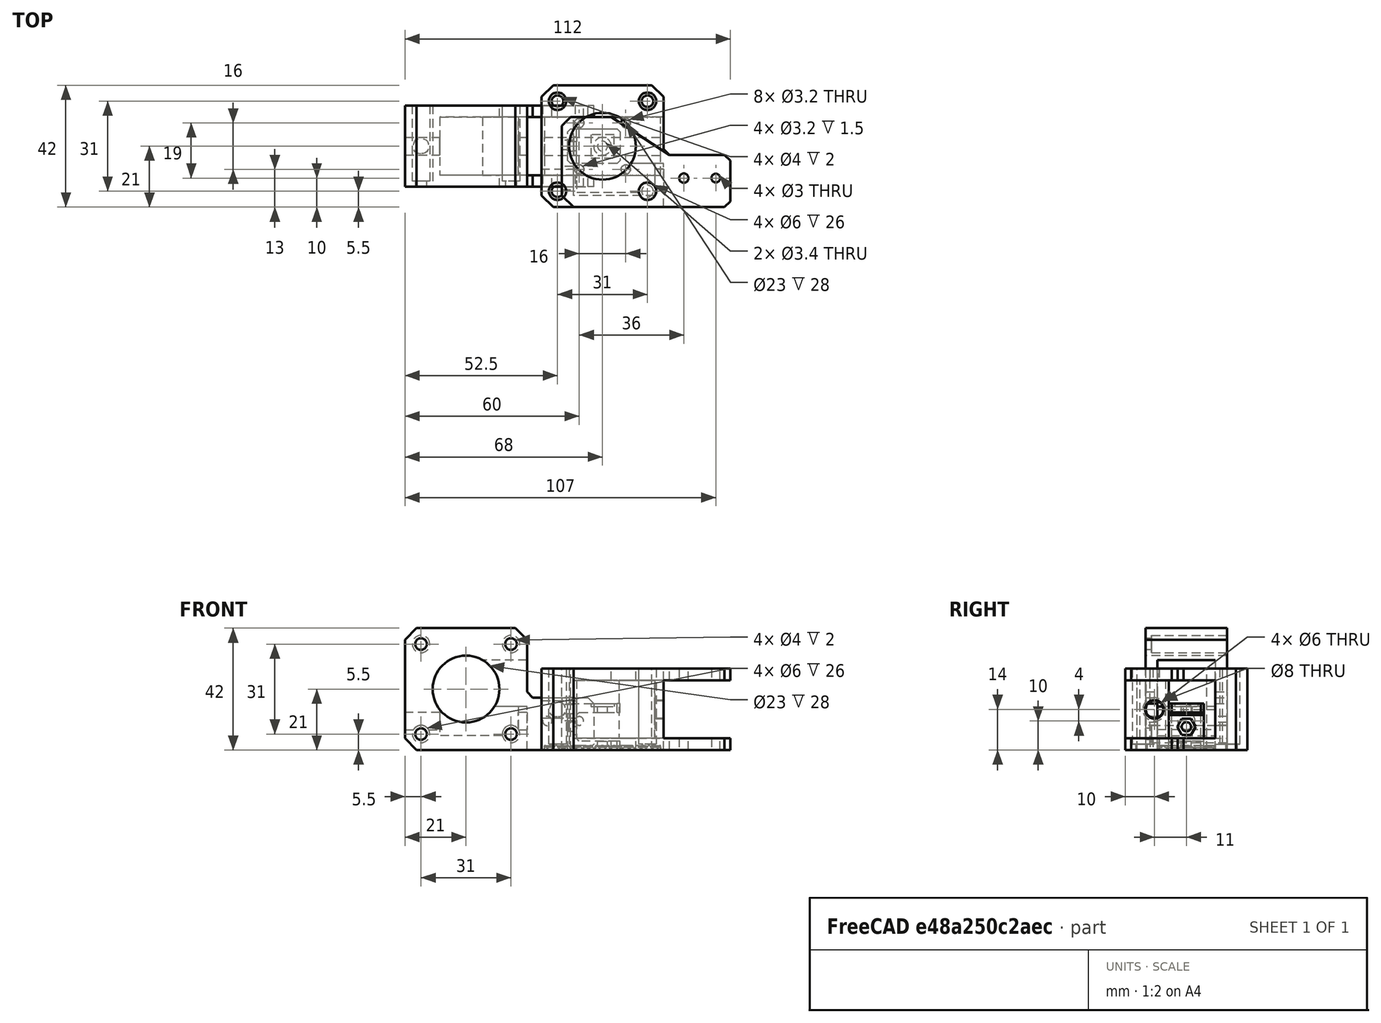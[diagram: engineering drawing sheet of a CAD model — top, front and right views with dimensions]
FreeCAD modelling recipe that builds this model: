
FCSTD DOCUMENT  (FreeCAD 1.0R39285 (Git))
Label: LinearRailMod
License: All rights reserved
LicenseURL: https://en.wikipedia.org/wiki/All_rights_reserved
objects: Sketcher::SketchObject×23, PartDesign::Pocket×18, PartDesign::Pad×5, PartDesign::Body×5, App::Part×5, Part::Mirroring×1, PartDesign::Hole×1, Assembly::JointGroup×1, Assembly::AssemblyObject×1
note: 124 computed .brp shape members not serialized (recipe doc carries the construction recipe); baked Part::Feature solids carry a one-line shape summary decoded from their .brp

FEATURE [Sketcher::SketchObject] Sketch
  ArcFitTolerance = 1e-06
  AttachmentSupport = -> [XY_Plane001]
  FullyConstrained = false
  MakeInternals = false
  MapMode = 5
  sketch-geometry (20):
    g0: GeomPoint [constr] X=0 Y=0 Z=0
    g1: LineSegment StartX=-17 StartY=21 StartZ=0 EndX=-21 EndY=17 EndZ=0
    g2: LineSegment StartX=-21 StartY=-17 StartZ=0 EndX=-17 EndY=-21 EndZ=0
    g3: LineSegment StartX=17 StartY=21 StartZ=0 EndX=21 EndY=17 EndZ=0
    g4: Circle CenterX=-15.5 CenterY=-15.5 CenterZ=0 NormalX=0 NormalY=0 NormalZ=1 AngleXU=0 Radius=2
    g5: Circle CenterX=15.5 CenterY=-15.5 CenterZ=0 NormalX=0 NormalY=0 NormalZ=1 AngleXU=0 Radius=2
    g6: Circle CenterX=15.5 CenterY=15.5 CenterZ=0 NormalX=0 NormalY=0 NormalZ=1 AngleXU=0 Radius=2
    g7: LineSegment StartX=-21 StartY=17 StartZ=0 EndX=-21 EndY=-17 EndZ=0
    g8: LineSegment StartX=-17 StartY=-21 StartZ=0 EndX=42 EndY=-21 EndZ=0
    g9: LineSegment StartX=-17 StartY=21 StartZ=0 EndX=17 EndY=21 EndZ=0
    g10: LineSegment StartX=21 StartY=17 StartZ=0 EndX=21 EndY=-1 EndZ=0
    g11: LineSegment StartX=44 StartY=-19 StartZ=0 EndX=42 EndY=-21 EndZ=0
    g12: Circle CenterX=-15.5 CenterY=15.5 CenterZ=0 NormalX=0 NormalY=0 NormalZ=1 AngleXU=0 Radius=2
    g13: Circle CenterX=0 CenterY=0 CenterZ=0 NormalX=0 NormalY=0 NormalZ=1 AngleXU=0 Radius=11.5
    g14: Circle CenterX=28 CenterY=-11 CenterZ=0 NormalX=0 NormalY=0 NormalZ=1 AngleXU=0 Radius=1.6
    g15: LineSegment StartX=21 StartY=-1 StartZ=0 EndX=23 EndY=-3 EndZ=0
    g16: LineSegment StartX=23 StartY=-3 StartZ=0 EndX=42 EndY=-3 EndZ=0
    g17: LineSegment StartX=42 StartY=-3 StartZ=0 EndX=44 EndY=-5 EndZ=0
    g18: LineSegment StartX=44 StartY=-5 StartZ=0 EndX=44 EndY=-19 EndZ=0
    g19: Circle CenterX=39 CenterY=-11 CenterZ=0 NormalX=0 NormalY=0 NormalZ=1 AngleXU=0 Radius=1.5
  constraints (19):
    c: Coincident(g7,g1)
    c: Coincident(g7,g2)
    c: Vertical(g7)
    c: Coincident(g8,g2)
    c: Horizontal(g8)
    c: Coincident(g9,g1)
    c: Coincident(g9,g3)
    c: Horizontal(g9)
    c: Coincident(g10,g3)
    c: Vertical(g10)
    c: Coincident(g11,g8)
    c: Coincident(g13,g0)
    c: Coincident(g15,g10)
    c: Coincident(g16,g15)
    c: Horizontal(g16)
    c: Coincident(g17,g16)
    c: Coincident(g18,g17)
    c: Coincident(g18,g11)
    c: Vertical(g18)
FEATURE [PartDesign::Pad] Pad
  Direction = (0,0,1)
  Length = 28
  Length2 = 10
  Profile = -> Sketch
  ReferenceAxis = -> Sketch [N_Axis]
  Refine = true
  Suppressed = false
  Type = 0
FEATURE [Sketcher::SketchObject] Sketch003
  ArcFitTolerance = 1e-06
  AttachmentSupport = -> [Pad]
  FullyConstrained = false
  MakeInternals = false
  MapMode = 5
  Placement = pos=(0,-21,0) rot=(1,0,0;1.5708rad)
  sketch-geometry (4):
    g0: LineSegment StartX=21 StartY=24 StartZ=0 EndX=21 EndY=4 EndZ=0
    g1: LineSegment StartX=21 StartY=4 StartZ=0 EndX=50 EndY=4 EndZ=0
    g2: LineSegment StartX=50 StartY=4 StartZ=0 EndX=50 EndY=24 EndZ=0
    g3: LineSegment StartX=50 StartY=24 StartZ=0 EndX=21 EndY=24 EndZ=0
  constraints (8):
    c: Coincident(g0,g1)
    c: Coincident(g1,g2)
    c: Coincident(g2,g3)
    c: Coincident(g3,g0)
    c: Vertical(g0)
    c: Vertical(g2)
    c: Horizontal(g1)
    c: Horizontal(g3)
FEATURE [PartDesign::Pocket] Pocket
  BaseFeature = -> Pad
  Direction = (0,1,-2e-16)
  Length = 42
  Length2 = 5
  Profile = -> Sketch003
  ReferenceAxis = -> Sketch003 [N_Axis]
  Refine = true
  Suppressed = false
  Type = 0
FEATURE [Sketcher::SketchObject] Sketch004
  ArcFitTolerance = 1e-06
  AttachmentSupport = -> [Pocket]
  FullyConstrained = false
  MakeInternals = false
  MapMode = 5
  Placement = pos=(0,0,28) rot=(0,0,1;0rad)
  sketch-geometry (4):
    g0: Circle CenterX=-15.5 CenterY=-15.5 CenterZ=0 NormalX=0 NormalY=0 NormalZ=1 AngleXU=0 Radius=3
    g1: Circle CenterX=-15.5 CenterY=15.5 CenterZ=0 NormalX=0 NormalY=0 NormalZ=1 AngleXU=0 Radius=3
    g2: Circle CenterX=15.5 CenterY=15.5 CenterZ=0 NormalX=0 NormalY=0 NormalZ=1 AngleXU=0 Radius=3
    g3: Circle CenterX=15.5 CenterY=-15.5 CenterZ=0 NormalX=0 NormalY=0 NormalZ=1 AngleXU=0 Radius=3
FEATURE [PartDesign::Pocket] Pocket001
  BaseFeature = -> Pocket
  Direction = (0,0,-1)
  Length = 26
  Length2 = 5
  Profile = -> Sketch004
  ReferenceAxis = -> Sketch004 [N_Axis]
  Refine = true
  Suppressed = false
  Type = 0
FEATURE [Sketcher::SketchObject] Sketch005
  ArcFitTolerance = 1e-06
  AttachmentSupport = -> [Pocket001]
  FullyConstrained = false
  MakeInternals = false
  MapMode = 5
  Placement = pos=(21,0,0) rot=(0.57735,0.57735,0.57735;2.0944rad)
  sketch-geometry (1):
    g0: Circle CenterX=-11 CenterY=14 CenterZ=0 NormalX=0 NormalY=0 NormalZ=1 AngleXU=0 Radius=3
FEATURE [PartDesign::Pocket] Pocket002
  BaseFeature = -> Pocket001
  Direction = (-1,0,0)
  Length = 42
  Length2 = 5
  Profile = -> Sketch005
  ReferenceAxis = -> Sketch005 [N_Axis]
  Refine = true
  Suppressed = false
  Type = 0
FEATURE [Sketcher::SketchObject] Sketch006
  ArcFitTolerance = 1e-06
  AttachmentSupport = -> [Pocket002]
  FullyConstrained = false
  MakeInternals = false
  MapMode = 5
  Placement = pos=(21,0,0) rot=(0.57735,0.57735,0.57735;2.0944rad)
  sketch-geometry (4):
    g0: LineSegment StartX=-6 StartY=24 StartZ=0 EndX=-6 EndY=4 EndZ=0
    g1: LineSegment StartX=-6 StartY=4 StartZ=0 EndX=10 EndY=4 EndZ=0
    g2: LineSegment StartX=10 StartY=4 StartZ=0 EndX=10 EndY=24 EndZ=0
    g3: LineSegment StartX=10 StartY=24 StartZ=0 EndX=-6 EndY=24 EndZ=0
  constraints (8):
    c: Coincident(g0,g1)
    c: Coincident(g1,g2)
    c: Coincident(g2,g3)
    c: Coincident(g3,g0)
    c: Vertical(g0)
    c: Vertical(g2)
    c: Horizontal(g1)
    c: Horizontal(g3)
FEATURE [PartDesign::Pocket] Pocket003
  BaseFeature = -> Pocket002
  Direction = (-1,0,0)
  Length = 16
  Length2 = 5
  Profile = -> Sketch006
  ReferenceAxis = -> Sketch006 [N_Axis]
  Refine = true
  Suppressed = false
  Type = 0
FEATURE [Sketcher::SketchObject] Sketch007
  ArcFitTolerance = 1e-06
  AttachmentSupport = -> [Pocket003]
  FullyConstrained = false
  MakeInternals = false
  MapMode = 5
  Placement = pos=(0,-6,0) rot=(0,0.707107,0.707107;3.14159rad)
  sketch-geometry (4):
    g0: LineSegment StartX=-18 StartY=24.038 StartZ=0 EndX=-18 EndY=4.03804 EndZ=0
    g1: LineSegment StartX=-18 StartY=4.03804 StartZ=0 EndX=9 EndY=4.03804 EndZ=0
    g2: LineSegment StartX=9 StartY=4.03804 StartZ=0 EndX=9 EndY=24.038 EndZ=0
    g3: LineSegment StartX=9 StartY=24.038 StartZ=0 EndX=-18 EndY=24.038 EndZ=0
  constraints (8):
    c: Coincident(g0,g1)
    c: Coincident(g1,g2)
    c: Coincident(g2,g3)
    c: Coincident(g3,g0)
    c: Vertical(g0)
    c: Vertical(g2)
    c: Horizontal(g1)
    c: Horizontal(g3)
FEATURE [PartDesign::Pocket] Pocket004
  BaseFeature = -> Pocket003
  Direction = (0,-1,2e-16)
  Length = 10
  Length2 = 5
  Profile = -> Sketch007
  ReferenceAxis = -> Sketch007 [N_Axis]
  Refine = true
  Suppressed = false
  Type = 0
FEATURE [PartDesign::Body] Body
  AllowCompound = false
  Group = -> [Sketch,Pad,Sketch003,Pocket,Sketch004,Pocket001,Sketch005,Pocket002,Sketch006,Pocket003,Sketch007,Pocket004]
  Origin = -> Origin001
  Tip = -> Pocket004
FEATURE [App::Part] Part  label="Motor"
  Group = -> [Body]
  Origin = -> Origin
  Placement = pos=(-47,-41,21) rot=(1,0,0;1.5708rad)
FEATURE [Sketcher::SketchObject] Sketch008
  ArcFitTolerance = 1e-06
  AttachmentSupport = -> [XY_Plane007]
  FullyConstrained = false
  MakeInternals = false
  MapMode = 5
  sketch-geometry (12):
    g0: LineSegment StartX=-14 StartY=-17 StartZ=0 EndX=-10 EndY=-21 EndZ=0
    g1: LineSegment StartX=-14 StartY=7 StartZ=0 EndX=-14 EndY=-17 EndZ=0
    g2: LineSegment StartX=-10 StartY=-21 StartZ=0 EndX=42 EndY=-21 EndZ=0
    g3: LineSegment StartX=44 StartY=-19 StartZ=0 EndX=42 EndY=-21 EndZ=0
    g4: Circle CenterX=28 CenterY=-11 CenterZ=0 NormalX=0 NormalY=0 NormalZ=1 AngleXU=0 Radius=1.6
    g5: LineSegment StartX=23 StartY=-3 StartZ=0 EndX=42 EndY=-3 EndZ=0
    g6: LineSegment StartX=42 StartY=-3 StartZ=0 EndX=44 EndY=-5 EndZ=0
    g7: LineSegment StartX=44 StartY=-5 StartZ=0 EndX=44 EndY=-19 EndZ=0
    g8: Circle CenterX=39 CenterY=-11 CenterZ=0 NormalX=0 NormalY=0 NormalZ=1 AngleXU=0 Radius=1.5
    g9: LineSegment StartX=23 StartY=-3 StartZ=0 EndX=3 EndY=10 EndZ=0
    g10: LineSegment StartX=3 StartY=10 StartZ=0 EndX=-11 EndY=10 EndZ=0
    g11: LineSegment StartX=-11 StartY=10 StartZ=0 EndX=-14 EndY=7 EndZ=0
  constraints (15):
    c: Coincident(g1,g0)
    c: Vertical(g1)
    c: Coincident(g2,g0)
    c: Horizontal(g2)
    c: Coincident(g3,g2)
    c: Horizontal(g5)
    c: Coincident(g6,g5)
    c: Coincident(g7,g6)
    c: Coincident(g7,g3)
    c: Vertical(g7)
    c: Coincident(g5,g9)
    c: Coincident(g9,g10)
    c: Horizontal(g10)
    c: Coincident(g10,g11)
    c: Coincident(g11,g1)
FEATURE [Sketcher::SketchObject] Sketch009
  ArcFitTolerance = 1e-06
  AttachmentSupport = -> [XY_Plane006]
  FullyConstrained = false
  MakeInternals = false
  MapMode = 5
  sketch-geometry (10):
    g0: Circle [constr] CenterX=0 CenterY=0 CenterZ=0 NormalX=0 NormalY=0 NormalZ=1 AngleXU=0 Radius=6.5
    g1: LineSegment StartX=-12 StartY=5 StartZ=0 EndX=-11 EndY=6 EndZ=0
    g2: LineSegment StartX=-11 StartY=6 StartZ=0 EndX=5 EndY=6 EndZ=0
    g3: LineSegment StartX=5 StartY=6 StartZ=0 EndX=6 EndY=5 EndZ=0
    g4: LineSegment StartX=6 StartY=5 StartZ=0 EndX=6 EndY=-5 EndZ=0
    g5: LineSegment StartX=6 StartY=-5 StartZ=0 EndX=5 EndY=-6 EndZ=0
    g6: LineSegment StartX=5 StartY=-6 StartZ=0 EndX=-11 EndY=-6 EndZ=0
    g7: LineSegment StartX=-11 StartY=-6 StartZ=0 EndX=-12 EndY=-5 EndZ=0
    g8: LineSegment StartX=-12 StartY=-5 StartZ=0 EndX=-12 EndY=5 EndZ=0
    g9: Circle CenterX=0 CenterY=0 CenterZ=0 NormalX=0 NormalY=0 NormalZ=1 AngleXU=0 Radius=1.6
  constraints (12):
    c: Coincident(g1,g2)
    c: Horizontal(g2)
    c: Coincident(g2,g3)
    c: Coincident(g3,g4)
    c: Vertical(g4)
    c: Coincident(g4,g5)
    c: Coincident(g5,g6)
    c: Horizontal(g6)
    c: Coincident(g6,g7)
    c: Coincident(g7,g8)
    c: Coincident(g8,g1)
    c: Vertical(g8)
FEATURE [Part::Mirroring] Part__Mirroring  label="Motor (Mirror #1)"
  Base = (0,0,0)
  Normal = (0,0,1)
  Placement = pos=(0,-55,2.04e-14) rot=(1,0,0;3.14159rad)
  Source = -> Part
FEATURE [PartDesign::Pad] Pad001
  Direction = (0,0,1)
  Length = 16
  Length2 = 10
  Profile = -> Sketch009
  ReferenceAxis = -> Sketch009 [N_Axis]
  Refine = true
  Suppressed = false
  Type = 0
FEATURE [Sketcher::SketchObject] Sketch013
  ArcFitTolerance = 1e-06
  FullyConstrained = false
  MakeInternals = false
  MapMode = 5
  Placement = pos=(0,-6,0) rot=(1,0,0;1.5708rad)
  sketch-geometry (6):
    g0: LineSegment StartX=-9 StartY=12 StartZ=0 EndX=-8 EndY=13 EndZ=0
    g1: LineSegment StartX=-8 StartY=13 StartZ=0 EndX=5 EndY=13 EndZ=0
    g2: LineSegment StartX=5 StartY=13 StartZ=0 EndX=5 EndY=3 EndZ=0
    g3: LineSegment StartX=5 StartY=3 StartZ=0 EndX=-8 EndY=3 EndZ=0
    g4: LineSegment StartX=-8 StartY=3 StartZ=0 EndX=-9 EndY=4 EndZ=0
    g5: LineSegment StartX=-9 StartY=4 StartZ=0 EndX=-9 EndY=12 EndZ=0
  constraints (10):
    c: Coincident(g0,g1)
    c: Horizontal(g1)
    c: Coincident(g1,g2)
    c: Vertical(g2)
    c: Coincident(g2,g3)
    c: Horizontal(g3)
    c: Coincident(g3,g4)
    c: Coincident(g4,g5)
    c: Coincident(g5,g0)
    c: Vertical(g5)
FEATURE [Sketcher::SketchObject] Sketch014
  ArcFitTolerance = 1e-06
  FullyConstrained = false
  MakeInternals = false
  MapMode = 5
  Placement = pos=(5,0,0) rot=(0.57735,-0.57735,-0.57735;2.0944rad)
  sketch-geometry (4):
    g0: LineSegment StartX=-6 StartY=13 StartZ=0 EndX=-6 EndY=3 EndZ=0
    g1: LineSegment StartX=-6 StartY=3 StartZ=0 EndX=6 EndY=3 EndZ=0
    g2: LineSegment StartX=6 StartY=3 StartZ=0 EndX=6 EndY=13 EndZ=0
    g3: LineSegment StartX=6 StartY=13 StartZ=0 EndX=-6 EndY=13 EndZ=0
  constraints (8):
    c: Coincident(g0,g1)
    c: Coincident(g1,g2)
    c: Coincident(g2,g3)
    c: Coincident(g3,g0)
    c: Vertical(g0)
    c: Vertical(g2)
    c: Horizontal(g1)
    c: Horizontal(g3)
FEATURE [PartDesign::Pocket] Pocket006
  BaseFeature = -> Pad001
  Direction = (0,1,-2e-16)
  Length = 12
  Length2 = 5
  Profile = -> Sketch013
  ReferenceAxis = -> Sketch013 [N_Axis]
  Refine = true
  Suppressed = false
  Type = 0
FEATURE [PartDesign::Pocket] Pocket007
  BaseFeature = -> Pocket006
  Direction = (1,-1e-16,1e-16)
  Length = 1
  Length2 = 5
  Profile = -> Sketch014
  ReferenceAxis = -> Sketch014 [N_Axis]
  Refine = true
  Suppressed = false
  Type = 0
FEATURE [Sketcher::SketchObject] Sketch015
  ArcFitTolerance = 1e-06
  AttachmentSupport = -> [Pocket007]
  FullyConstrained = false
  MakeInternals = false
  MapMode = 5
  Placement = pos=(-12,0,0) rot=(0.57735,-0.57735,-0.57735;2.0944rad)
  sketch-geometry (1):
    g0: Circle CenterX=0 CenterY=8 CenterZ=0 NormalX=0 NormalY=0 NormalZ=1 AngleXU=0 Radius=1.6
FEATURE [PartDesign::Pocket] Pocket008
  BaseFeature = -> Pocket007
  Direction = (1,0,0)
  Length = 3
  Length2 = 5
  Profile = -> Sketch015
  ReferenceAxis = -> Sketch015 [N_Axis]
  Refine = true
  Suppressed = false
  Type = 0
FEATURE [Sketcher::SketchObject] Sketch016
  ArcFitTolerance = 1e-06
  AttachmentSupport = -> [Pocket008]
  FullyConstrained = false
  MakeInternals = false
  MapMode = 5
  Placement = pos=(0,0,16) rot=(0,0,1;0rad)
  sketch-geometry (5):
    g0: LineSegment StartX=-4 StartY=-4 StartZ=0 EndX=4 EndY=-4 EndZ=0
    g1: LineSegment StartX=4 StartY=-4 StartZ=0 EndX=4 EndY=4 EndZ=0
    g2: LineSegment StartX=4 StartY=4 StartZ=0 EndX=-4 EndY=4 EndZ=0
    g3: LineSegment StartX=-4 StartY=4 StartZ=0 EndX=-4 EndY=-4 EndZ=0
    g4: GeomPoint [constr] X=0 Y=0 Z=0
  constraints (10):
    c: Coincident(g0,g1)
    c: Coincident(g1,g2)
    c: Coincident(g2,g3)
    c: Coincident(g3,g0)
    c: Horizontal(g0)
    c: Horizontal(g2)
    c: Vertical(g1)
    c: Vertical(g3)
    c: Symmetric(g2,g0,g4)
    c: Coincident(g4,g-1)
FEATURE [PartDesign::Pocket] Pocket009
  BaseFeature = -> Pocket008
  Direction = (0,0,-1)
  Length = 1
  Length2 = 5
  Profile = -> Sketch016
  ReferenceAxis = -> Sketch016 [N_Axis]
  Refine = true
  Suppressed = false
  Type = 0
FEATURE [Sketcher::SketchObject] Sketch017
  ArcFitTolerance = 1e-06
  AttachmentSupport = -> [Pocket009]
  FullyConstrained = false
  MakeInternals = false
  MapMode = 5
  Placement = pos=(-9,0,0) rot=(0.57735,0.57735,0.57735;2.0944rad)
  sketch-geometry (7):
    g0: LineSegment StartX=3.2 StartY=8 StartZ=0 EndX=1.6 EndY=10.7713 EndZ=0
    g1: LineSegment StartX=1.6 StartY=10.7713 StartZ=0 EndX=-1.6 EndY=10.7713 EndZ=0
    g2: LineSegment StartX=-1.6 StartY=10.7713 StartZ=0 EndX=-3.2 EndY=8 EndZ=0
    g3: LineSegment StartX=-3.2 StartY=8 StartZ=0 EndX=-1.6 EndY=5.22872 EndZ=0
    g4: LineSegment StartX=-1.6 StartY=5.22872 StartZ=0 EndX=1.6 EndY=5.22872 EndZ=0
    g5: LineSegment StartX=1.6 StartY=5.22872 StartZ=0 EndX=3.2 EndY=8 EndZ=0
    g6: Circle [constr] CenterX=0 CenterY=8 CenterZ=0 NormalX=0 NormalY=0 NormalZ=1 AngleXU=0 Radius=3.2
  constraints (13):
    c: Coincident(g0,g1)
    c: Coincident(g1,g2)
    c: Coincident(g2,g3)
    c: Coincident(g3,g4)
    c: Coincident(g4,g5)
    c: Coincident(g5,g0)
    c: Equal(g0, g1-g5) x5
    c: PointOnObject(g0,g6)
    c: PointOnObject(g1,g6)
    c: PointOnObject(g2,g6)
    c: PointOnObject(g3,g6)
    c: PointOnObject(g4,g6)
    c: PointOnObject(g5,g6)
FEATURE [PartDesign::Pocket] Pocket010
  BaseFeature = -> Pocket009
  Direction = (-1,0,0)
  Length = 1
  Length2 = 5
  Profile = -> Sketch017
  ReferenceAxis = -> Sketch017 [N_Axis]
  Refine = true
  Suppressed = false
  Type = 0
FEATURE [PartDesign::Hole] Hole
  BaseFeature = -> Pocket010
  CustomThreadClearance = 0
  Depth = 25
  DepthType = 0
  Diameter = 3.4
  DrillForDepth = false
  DrillPoint = 1
  DrillPointAngle = 118
  HoleCutCountersinkAngle = 90
  HoleCutCustomValues = false
  HoleCutDepth = 0
  HoleCutDiameter = 6.1
  HoleCutType = 2
  ModelThread = false
  Profile = -> Pocket010 [Face4]
  Refine = true
  Suppressed = false
  Tapered = false
  TaperedAngle = 90
  ThreadClass = 0
  ThreadDepth = 25
  ThreadDepthType = 0
  ThreadDirection = 0
  ThreadFit = 0
  ThreadSize = 9
  ThreadType = 1
  Threaded = false
  UseCustomThreadClearance = false
FEATURE [PartDesign::Body] Body001
  AllowCompound = false
  Group = -> [Sketch009,Pad001,Sketch013,Sketch014,Pocket006,Pocket007,Sketch015,Pocket008,Sketch016,Pocket009,Sketch017,Pocket010,Hole]
  Origin = -> Origin006
  Tip = -> Hole
FEATURE [App::Part] Part002  label="IdlerGear"
  Group = -> [Body001]
  Origin = -> Origin005
  Placement = pos=(37,-8,22) rot=(0,0.707107,0.707107;3.14159rad)
FEATURE [PartDesign::Pad] Pad002
  Direction = (0,0,1)
  Length = 28
  Length2 = 10
  Profile = -> Sketch008
  ReferenceAxis = -> Sketch008 [N_Axis]
  Refine = true
  Suppressed = false
  Type = 0
FEATURE [Sketcher::SketchObject] Sketch018
  ArcFitTolerance = 1e-06
  AttachmentSupport = -> [Pad002]
  FullyConstrained = false
  MakeInternals = false
  MapMode = 5
  Placement = pos=(0,-21,0) rot=(1,0,0;1.5708rad)
  sketch-geometry (4):
    g0: LineSegment StartX=21 StartY=24 StartZ=0 EndX=21 EndY=4 EndZ=0
    g1: LineSegment StartX=21 StartY=4 StartZ=0 EndX=50 EndY=4 EndZ=0
    g2: LineSegment StartX=50 StartY=4 StartZ=0 EndX=50 EndY=24 EndZ=0
    g3: LineSegment StartX=50 StartY=24 StartZ=0 EndX=21 EndY=24 EndZ=0
  constraints (8):
    c: Coincident(g0,g1)
    c: Coincident(g1,g2)
    c: Coincident(g2,g3)
    c: Coincident(g3,g0)
    c: Vertical(g0)
    c: Vertical(g2)
    c: Horizontal(g1)
    c: Horizontal(g3)
FEATURE [PartDesign::Pocket] Pocket011
  BaseFeature = -> Pad002
  Direction = (0,1,-2e-16)
  Length = 42
  Length2 = 5
  Profile = -> Sketch018
  ReferenceAxis = -> Sketch018 [N_Axis]
  Refine = true
  Suppressed = false
  Type = 0
FEATURE [Sketcher::SketchObject] Sketch020
  ArcFitTolerance = 1e-06
  FullyConstrained = false
  MakeInternals = false
  MapMode = 5
  Placement = pos=(21,0,0) rot=(0.57735,0.57735,0.57735;2.0944rad)
  sketch-geometry (4):
    g0: LineSegment StartX=-6 StartY=24 StartZ=0 EndX=-6 EndY=4 EndZ=0
    g1: LineSegment StartX=-6 StartY=4 StartZ=0 EndX=17 EndY=4 EndZ=0
    g2: LineSegment StartX=17 StartY=4 StartZ=0 EndX=17 EndY=24 EndZ=0
    g3: LineSegment StartX=17 StartY=24 StartZ=0 EndX=-6 EndY=24 EndZ=0
  constraints (8):
    c: Coincident(g0,g1)
    c: Coincident(g1,g2)
    c: Coincident(g2,g3)
    c: Coincident(g3,g0)
    c: Vertical(g0)
    c: Vertical(g2)
    c: Horizontal(g1)
    c: Horizontal(g3)
FEATURE [PartDesign::Pocket] Pocket013
  BaseFeature = -> Pocket011
  Direction = (-1,0,0)
  Length = 31
  Length2 = 5
  Profile = -> Sketch020
  ReferenceAxis = -> Sketch020 [N_Axis]
  Refine = true
  Suppressed = false
  Type = 0
FEATURE [Sketcher::SketchObject] Sketch021
  ArcFitTolerance = 1e-06
  AttachmentSupport = -> [Pocket013]
  FullyConstrained = false
  MakeInternals = false
  MapMode = 5
  Placement = pos=(0,-6,0) rot=(0,0.707107,0.707107;3.14159rad)
  sketch-geometry (4):
    g0: LineSegment StartX=10 StartY=24 StartZ=0 EndX=-18 EndY=24 EndZ=0
    g1: LineSegment StartX=-18 StartY=24 StartZ=0 EndX=-18 EndY=4 EndZ=0
    g2: LineSegment StartX=-18 StartY=4 StartZ=0 EndX=10 EndY=4 EndZ=0
    g3: LineSegment StartX=10 StartY=4 StartZ=0 EndX=10 EndY=24 EndZ=0
  constraints (8):
    c: Coincident(g0,g1)
    c: Coincident(g1,g2)
    c: Coincident(g2,g3)
    c: Coincident(g3,g0)
    c: Horizontal(g0)
    c: Horizontal(g2)
    c: Vertical(g1)
    c: Vertical(g3)
FEATURE [PartDesign::Pocket] Pocket014
  BaseFeature = -> Pocket013
  Direction = (0,-1,2e-16)
  Length = 11
  Length2 = 5
  Profile = -> Sketch021
  ReferenceAxis = -> Sketch021 [N_Axis]
  Refine = true
  Suppressed = false
  Type = 0
FEATURE [Sketcher::SketchObject] Sketch022
  ArcFitTolerance = 1e-06
  AttachmentSupport = -> [Pocket014]
  FullyConstrained = false
  MakeInternals = false
  MapMode = 5
  Placement = pos=(21,0,0) rot=(0.57735,0.57735,0.57735;2.0944rad)
  sketch-geometry (1):
    g0: Circle CenterX=-11 CenterY=14 CenterZ=0 NormalX=0 NormalY=0 NormalZ=1 AngleXU=0 Radius=3.2
FEATURE [PartDesign::Pocket] Pocket015
  BaseFeature = -> Pocket014
  Direction = (-1,0,0)
  Length = 5
  Length2 = 5
  Profile = -> Sketch022
  ReferenceAxis = -> Sketch022 [N_Axis]
  Refine = true
  Suppressed = false
  Type = 0
FEATURE [Sketcher::SketchObject] Sketch023
  ArcFitTolerance = 1e-06
  AttachmentSupport = -> [Pocket015]
  FullyConstrained = false
  MakeInternals = false
  MapMode = 5
  Placement = pos=(-14,0,0) rot=(0.57735,-0.57735,-0.57735;2.0944rad)
  sketch-geometry (2):
    g0: Circle CenterX=11 CenterY=14 CenterZ=0 NormalX=0 NormalY=0 NormalZ=1 AngleXU=0 Radius=4
    g1: Circle CenterX=-0.5 CenterY=14 CenterZ=0 NormalX=0 NormalY=0 NormalZ=1 AngleXU=0 Radius=1.6
FEATURE [PartDesign::Pocket] Pocket016
  BaseFeature = -> Pocket015
  Direction = (1,0,0)
  Length = 5
  Length2 = 5
  Profile = -> Sketch023
  ReferenceAxis = -> Sketch023 [N_Axis]
  Refine = true
  Suppressed = false
  Type = 0
FEATURE [PartDesign::Body] Body002
  AllowCompound = false
  Group = -> [Sketch008,Pad002,Sketch018,Pocket011,Sketch020,Pocket013,Sketch021,Pocket014,Sketch022,Pocket015,Sketch023,Pocket016]
  Origin = -> Origin007
  Tip = -> Pocket016
FEATURE [App::Part] Part001  label="IdlerGearFrame"
  Group = -> [Body002]
  Origin = -> Origin004
  Placement = pos=(44,-14,21) rot=(0,-0.707107,-0.707107;3.14159rad)
FEATURE [Sketcher::SketchObject] Sketch024
  ArcFitTolerance = 1e-06
  AttachmentSupport = -> [XY_Plane010]
  FullyConstrained = false
  MakeInternals = false
  MapMode = 5
  sketch-geometry (5):
    g0: LineSegment StartX=-20 StartY=10 StartZ=0 EndX=-20 EndY=-10 EndZ=0
    g1: LineSegment StartX=-20 StartY=-10 StartZ=0 EndX=20 EndY=-10 EndZ=0
    g2: LineSegment StartX=20 StartY=-10 StartZ=0 EndX=20 EndY=10 EndZ=0
    g3: LineSegment StartX=20 StartY=10 StartZ=0 EndX=-20 EndY=10 EndZ=0
    g4: GeomPoint [constr] X=0 Y=0 Z=0
  constraints (9):
    c: Coincident(g0,g1)
    c: Coincident(g1,g2)
    c: Coincident(g2,g3)
    c: Coincident(g3,g0)
    c: Vertical(g0)
    c: Vertical(g2)
    c: Horizontal(g1)
    c: Horizontal(g3)
    c: Symmetric(g2,g0,g4)
FEATURE [PartDesign::Pad] Pad003
  Direction = (0,0,1)
  Length = 1.5
  Length2 = 10
  Profile = -> Sketch024
  ReferenceAxis = -> Sketch024 [N_Axis]
  Refine = true
  Suppressed = false
  Type = 0
FEATURE [Sketcher::SketchObject] Sketch025
  ArcFitTolerance = 1e-06
  AttachmentSupport = -> [Pad003]
  FullyConstrained = false
  MakeInternals = false
  MapMode = 5
  Placement = pos=(0,-10,0) rot=(1,0,0;1.5708rad)
  sketch-geometry (120):
    g0: ArcOfCircle CenterX=-19.7402 CenterY=1.35 CenterZ=0 NormalX=0 NormalY=0 NormalZ=1 AngleXU=0 Radius=0.149997 StartAngle=0.134719 EndAngle=1.57082
    g1: ArcOfCircle CenterX=-18.2598 CenterY=1.35 CenterZ=0 NormalX=0 NormalY=0 NormalZ=1 AngleXU=0 Radius=0.15 StartAngle=1.5708 EndAngle=3.01411
    g2: ArcOfCircle CenterX=-19 CenterY=1.30511 CenterZ=0 NormalX=0 NormalY=0 NormalZ=1 AngleXU=0 Radius=0.555048 StartAngle=3.59519 EndAngle=5.83002
    g3: ArcOfCircle CenterX=-19.4 CenterY=1.5 CenterZ=0 NormalX=0 NormalY=0 NormalZ=1 AngleXU=0 Radius=1 StartAngle=5.82992 EndAngle=6.15188
    g4: ArcOfCircle CenterX=-18.6 CenterY=1.5 CenterZ=0 NormalX=0 NormalY=0 NormalZ=1 AngleXU=0 Radius=1 StartAngle=3.27181 EndAngle=3.5951
    g5: LineSegment StartX=-19.7402 StartY=1.5 StartZ=0 EndX=-18.2598 EndY=1.5 EndZ=0
    g6: ArcOfCircle CenterX=-17.7402 CenterY=1.35 CenterZ=0 NormalX=0 NormalY=0 NormalZ=1 AngleXU=0 Radius=0.149997 StartAngle=0.134719 EndAngle=1.57082
    g7: ArcOfCircle CenterX=-16.2598 CenterY=1.35 CenterZ=0 NormalX=0 NormalY=0 NormalZ=1 AngleXU=0 Radius=0.15 StartAngle=1.5708 EndAngle=3.01411
    g8: ArcOfCircle CenterX=-17 CenterY=1.30511 CenterZ=0 NormalX=0 NormalY=0 NormalZ=1 AngleXU=0 Radius=0.555048 StartAngle=3.59519 EndAngle=5.83002
    g9: ArcOfCircle CenterX=-17.4 CenterY=1.5 CenterZ=0 NormalX=0 NormalY=0 NormalZ=1 AngleXU=0 Radius=1 StartAngle=5.82992 EndAngle=6.15188
    g10: ArcOfCircle CenterX=-16.6 CenterY=1.5 CenterZ=0 NormalX=0 NormalY=0 NormalZ=1 AngleXU=0 Radius=1 StartAngle=3.27181 EndAngle=3.5951
    g11: LineSegment StartX=-17.7402 StartY=1.5 StartZ=0 EndX=-16.2598 EndY=1.5 EndZ=0
    g12: ArcOfCircle CenterX=-15.7402 CenterY=1.35 CenterZ=0 NormalX=0 NormalY=0 NormalZ=1 AngleXU=0 Radius=0.149997 StartAngle=0.134719 EndAngle=1.57082
    g13: ArcOfCircle CenterX=-14.2598 CenterY=1.35 CenterZ=0 NormalX=0 NormalY=0 NormalZ=1 AngleXU=0 Radius=0.15 StartAngle=1.5708 EndAngle=3.01411
    g14: ArcOfCircle CenterX=-15 CenterY=1.30511 CenterZ=0 NormalX=0 NormalY=0 NormalZ=1 AngleXU=0 Radius=0.555048 StartAngle=3.59519 EndAngle=5.83002
    g15: ArcOfCircle CenterX=-15.4 CenterY=1.5 CenterZ=0 NormalX=0 NormalY=0 NormalZ=1 AngleXU=0 Radius=1 StartAngle=5.82992 EndAngle=6.15188
    g16: ArcOfCircle CenterX=-14.6 CenterY=1.5 CenterZ=0 NormalX=0 NormalY=0 NormalZ=1 AngleXU=0 Radius=1 StartAngle=3.27181 EndAngle=3.5951
    g17: LineSegment StartX=-15.7402 StartY=1.5 StartZ=0 EndX=-14.2598 EndY=1.5 EndZ=0
    g18: ArcOfCircle CenterX=-13.7402 CenterY=1.35 CenterZ=0 NormalX=0 NormalY=0 NormalZ=1 AngleXU=0 Radius=0.149997 StartAngle=0.134719 EndAngle=1.57082
    g19: ArcOfCircle CenterX=-12.2598 CenterY=1.35 CenterZ=0 NormalX=0 NormalY=0 NormalZ=1 AngleXU=0 Radius=0.15 StartAngle=1.5708 EndAngle=3.01411
    g20: ArcOfCircle CenterX=-13 CenterY=1.30511 CenterZ=0 NormalX=0 NormalY=0 NormalZ=1 AngleXU=0 Radius=0.555048 StartAngle=3.59519 EndAngle=5.83002
    g21: ArcOfCircle CenterX=-13.4 CenterY=1.5 CenterZ=0 NormalX=0 NormalY=0 NormalZ=1 AngleXU=0 Radius=1 StartAngle=5.82992 EndAngle=6.15188
    g22: ArcOfCircle CenterX=-12.6 CenterY=1.5 CenterZ=0 NormalX=0 NormalY=0 NormalZ=1 AngleXU=0 Radius=1 StartAngle=3.27181 EndAngle=3.5951
    g23: LineSegment StartX=-13.7402 StartY=1.5 StartZ=0 EndX=-12.2598 EndY=1.5 EndZ=0
    g24: ArcOfCircle CenterX=-11.7402 CenterY=1.35 CenterZ=0 NormalX=0 NormalY=0 NormalZ=1 AngleXU=0 Radius=0.149997 StartAngle=0.134719 EndAngle=1.57082
    g25: ArcOfCircle CenterX=-10.2598 CenterY=1.35 CenterZ=0 NormalX=0 NormalY=0 NormalZ=1 AngleXU=0 Radius=0.15 StartAngle=1.5708 EndAngle=3.01411
    g26: ArcOfCircle CenterX=-11 CenterY=1.30511 CenterZ=0 NormalX=0 NormalY=0 NormalZ=1 AngleXU=0 Radius=0.555048 StartAngle=3.59519 EndAngle=5.83002
    g27: ArcOfCircle CenterX=-11.4 CenterY=1.5 CenterZ=0 NormalX=0 NormalY=0 NormalZ=1 AngleXU=0 Radius=1 StartAngle=5.82992 EndAngle=6.15188
    g28: ArcOfCircle CenterX=-10.6 CenterY=1.5 CenterZ=0 NormalX=0 NormalY=0 NormalZ=1 AngleXU=0 Radius=1 StartAngle=3.27181 EndAngle=3.5951
    g29: LineSegment StartX=-11.7402 StartY=1.5 StartZ=0 EndX=-10.2598 EndY=1.5 EndZ=0
    g30: ArcOfCircle CenterX=-9.74017 CenterY=1.35 CenterZ=0 NormalX=0 NormalY=0 NormalZ=1 AngleXU=0 Radius=0.149997 StartAngle=0.134719 EndAngle=1.57082
    g31: ArcOfCircle CenterX=-8.25982 CenterY=1.35 CenterZ=0 NormalX=0 NormalY=0 NormalZ=1 AngleXU=0 Radius=0.15 StartAngle=1.5708 EndAngle=3.01411
    g32: ArcOfCircle CenterX=-9 CenterY=1.30511 CenterZ=0 NormalX=0 NormalY=0 NormalZ=1 AngleXU=0 Radius=0.555048 StartAngle=3.59519 EndAngle=5.83002
    g33: ArcOfCircle CenterX=-9.4 CenterY=1.5 CenterZ=0 NormalX=0 NormalY=0 NormalZ=1 AngleXU=0 Radius=1 StartAngle=5.82992 EndAngle=6.15188
    g34: ArcOfCircle CenterX=-8.6 CenterY=1.5 CenterZ=0 NormalX=0 NormalY=0 NormalZ=1 AngleXU=0 Radius=1 StartAngle=3.27181 EndAngle=3.5951
    g35: LineSegment StartX=-9.74018 StartY=1.5 StartZ=0 EndX=-8.25982 EndY=1.5 EndZ=0
    g36: ArcOfCircle CenterX=-7.74017 CenterY=1.35 CenterZ=0 NormalX=0 NormalY=0 NormalZ=1 AngleXU=0 Radius=0.149997 StartAngle=0.134719 EndAngle=1.57082
    g37: ArcOfCircle CenterX=-6.25982 CenterY=1.35 CenterZ=0 NormalX=0 NormalY=0 NormalZ=1 AngleXU=0 Radius=0.15 StartAngle=1.5708 EndAngle=3.01411
    g38: ArcOfCircle CenterX=-7 CenterY=1.30511 CenterZ=0 NormalX=0 NormalY=0 NormalZ=1 AngleXU=0 Radius=0.555048 StartAngle=3.59519 EndAngle=5.83002
    g39: ArcOfCircle CenterX=-7.4 CenterY=1.5 CenterZ=0 NormalX=0 NormalY=0 NormalZ=1 AngleXU=0 Radius=1 StartAngle=5.82992 EndAngle=6.15188
    g40: ArcOfCircle CenterX=-6.6 CenterY=1.5 CenterZ=0 NormalX=0 NormalY=0 NormalZ=1 AngleXU=0 Radius=1 StartAngle=3.27181 EndAngle=3.5951
    g41: LineSegment StartX=-7.74018 StartY=1.5 StartZ=0 EndX=-6.25982 EndY=1.5 EndZ=0
    g42: ArcOfCircle CenterX=-5.74017 CenterY=1.35 CenterZ=0 NormalX=0 NormalY=0 NormalZ=1 AngleXU=0 Radius=0.149997 StartAngle=0.134719 EndAngle=1.57082
    g43: ArcOfCircle CenterX=-4.25982 CenterY=1.35 CenterZ=0 NormalX=0 NormalY=0 NormalZ=1 AngleXU=0 Radius=0.15 StartAngle=1.5708 EndAngle=3.01411
    g44: ArcOfCircle CenterX=-5 CenterY=1.30511 CenterZ=0 NormalX=0 NormalY=0 NormalZ=1 AngleXU=0 Radius=0.555048 StartAngle=3.59519 EndAngle=5.83002
    g45: ArcOfCircle CenterX=-5.4 CenterY=1.5 CenterZ=0 NormalX=0 NormalY=0 NormalZ=1 AngleXU=0 Radius=1 StartAngle=5.82992 EndAngle=6.15188
    g46: ArcOfCircle CenterX=-4.6 CenterY=1.5 CenterZ=0 NormalX=0 NormalY=0 NormalZ=1 AngleXU=0 Radius=1 StartAngle=3.27181 EndAngle=3.5951
    g47: LineSegment StartX=-5.74018 StartY=1.5 StartZ=0 EndX=-4.25982 EndY=1.5 EndZ=0
    g48: ArcOfCircle CenterX=-3.74017 CenterY=1.35 CenterZ=0 NormalX=0 NormalY=0 NormalZ=1 AngleXU=0 Radius=0.149997 StartAngle=0.134719 EndAngle=1.57082
    g49: ArcOfCircle CenterX=-2.25982 CenterY=1.35 CenterZ=0 NormalX=0 NormalY=0 NormalZ=1 AngleXU=0 Radius=0.15 StartAngle=1.5708 EndAngle=3.01411
    g50: ArcOfCircle CenterX=-3 CenterY=1.30511 CenterZ=0 NormalX=0 NormalY=0 NormalZ=1 AngleXU=0 Radius=0.555048 StartAngle=3.59519 EndAngle=5.83002
    g51: ArcOfCircle CenterX=-3.4 CenterY=1.5 CenterZ=0 NormalX=0 NormalY=0 NormalZ=1 AngleXU=0 Radius=1 StartAngle=5.82992 EndAngle=6.15188
    g52: ArcOfCircle CenterX=-2.6 CenterY=1.5 CenterZ=0 NormalX=0 NormalY=0 NormalZ=1 AngleXU=0 Radius=1 StartAngle=3.27181 EndAngle=3.5951
    g53: LineSegment StartX=-3.74018 StartY=1.5 StartZ=0 EndX=-2.25982 EndY=1.5 EndZ=0
    g54: ArcOfCircle CenterX=-1.74017 CenterY=1.35 CenterZ=0 NormalX=0 NormalY=0 NormalZ=1 AngleXU=0 Radius=0.149997 StartAngle=0.134719 EndAngle=1.57082
    g55: ArcOfCircle CenterX=-0.259824 CenterY=1.35 CenterZ=0 NormalX=0 NormalY=0 NormalZ=1 AngleXU=0 Radius=0.15 StartAngle=1.5708 EndAngle=3.01411
    g56: ArcOfCircle CenterX=-1 CenterY=1.30511 CenterZ=0 NormalX=0 NormalY=0 NormalZ=1 AngleXU=0 Radius=0.555048 StartAngle=3.59519 EndAngle=5.83002
    g57: ArcOfCircle CenterX=-1.4 CenterY=1.5 CenterZ=0 NormalX=0 NormalY=0 NormalZ=1 AngleXU=0 Radius=1 StartAngle=5.82992 EndAngle=6.15188
    g58: ArcOfCircle CenterX=-0.599999 CenterY=1.5 CenterZ=0 NormalX=0 NormalY=0 NormalZ=1 AngleXU=0 Radius=1 StartAngle=3.27181 EndAngle=3.5951
    g59: LineSegment StartX=-1.74018 StartY=1.5 StartZ=0 EndX=-0.259824 EndY=1.5 EndZ=0
    g60: ArcOfCircle CenterX=0.259827 CenterY=1.35 CenterZ=0 NormalX=0 NormalY=0 NormalZ=1 AngleXU=0 Radius=0.149997 StartAngle=0.134719 EndAngle=1.57082
    g61: ArcOfCircle CenterX=1.74018 CenterY=1.35 CenterZ=0 NormalX=0 NormalY=0 NormalZ=1 AngleXU=0 Radius=0.15 StartAngle=1.5708 EndAngle=3.01411
    g62: ArcOfCircle CenterX=1 CenterY=1.30511 CenterZ=0 NormalX=0 NormalY=0 NormalZ=1 AngleXU=0 Radius=0.555048 StartAngle=3.59519 EndAngle=5.83002
    g63: ArcOfCircle CenterX=0.599998 CenterY=1.5 CenterZ=0 NormalX=0 NormalY=0 NormalZ=1 AngleXU=0 Radius=1 StartAngle=5.82992 EndAngle=6.15188
    g64: ArcOfCircle CenterX=1.4 CenterY=1.5 CenterZ=0 NormalX=0 NormalY=0 NormalZ=1 AngleXU=0 Radius=1 StartAngle=3.27181 EndAngle=3.5951
    g65: LineSegment StartX=0.259824 StartY=1.5 StartZ=0 EndX=1.74018 EndY=1.5 EndZ=0
    g66: ArcOfCircle CenterX=2.25983 CenterY=1.35 CenterZ=0 NormalX=0 NormalY=0 NormalZ=1 AngleXU=0 Radius=0.149997 StartAngle=0.134719 EndAngle=1.57082
    g67: ArcOfCircle CenterX=3.74018 CenterY=1.35 CenterZ=0 NormalX=0 NormalY=0 NormalZ=1 AngleXU=0 Radius=0.15 StartAngle=1.5708 EndAngle=3.01411
    g68: ArcOfCircle CenterX=3 CenterY=1.30511 CenterZ=0 NormalX=0 NormalY=0 NormalZ=1 AngleXU=0 Radius=0.555048 StartAngle=3.59519 EndAngle=5.83002
    g69: ArcOfCircle CenterX=2.6 CenterY=1.5 CenterZ=0 NormalX=0 NormalY=0 NormalZ=1 AngleXU=0 Radius=1 StartAngle=5.82992 EndAngle=6.15188
    g70: ArcOfCircle CenterX=3.4 CenterY=1.5 CenterZ=0 NormalX=0 NormalY=0 NormalZ=1 AngleXU=0 Radius=1 StartAngle=3.27181 EndAngle=3.5951
    g71: LineSegment StartX=2.25982 StartY=1.5 StartZ=0 EndX=3.74018 EndY=1.5 EndZ=0
    g72: ArcOfCircle CenterX=4.25983 CenterY=1.35 CenterZ=0 NormalX=0 NormalY=0 NormalZ=1 AngleXU=0 Radius=0.149997 StartAngle=0.134719 EndAngle=1.57082
    g73: ArcOfCircle CenterX=5.74018 CenterY=1.35 CenterZ=0 NormalX=0 NormalY=0 NormalZ=1 AngleXU=0 Radius=0.15 StartAngle=1.5708 EndAngle=3.01411
    g74: ArcOfCircle CenterX=5 CenterY=1.30511 CenterZ=0 NormalX=0 NormalY=0 NormalZ=1 AngleXU=0 Radius=0.555048 StartAngle=3.59519 EndAngle=5.83002
    g75: ArcOfCircle CenterX=4.6 CenterY=1.5 CenterZ=0 NormalX=0 NormalY=0 NormalZ=1 AngleXU=0 Radius=1 StartAngle=5.82992 EndAngle=6.15188
    g76: ArcOfCircle CenterX=5.4 CenterY=1.5 CenterZ=0 NormalX=0 NormalY=0 NormalZ=1 AngleXU=0 Radius=1 StartAngle=3.27181 EndAngle=3.5951
    g77: LineSegment StartX=4.25982 StartY=1.5 StartZ=0 EndX=5.74018 EndY=1.5 EndZ=0
    g78: ArcOfCircle CenterX=6.25983 CenterY=1.35 CenterZ=0 NormalX=0 NormalY=0 NormalZ=1 AngleXU=0 Radius=0.149997 StartAngle=0.134719 EndAngle=1.57082
    g79: ArcOfCircle CenterX=7.74018 CenterY=1.35 CenterZ=0 NormalX=0 NormalY=0 NormalZ=1 AngleXU=0 Radius=0.15 StartAngle=1.5708 EndAngle=3.01411
    g80: ArcOfCircle CenterX=7 CenterY=1.30511 CenterZ=0 NormalX=0 NormalY=0 NormalZ=1 AngleXU=0 Radius=0.555048 StartAngle=3.59519 EndAngle=5.83002
    g81: ArcOfCircle CenterX=6.6 CenterY=1.5 CenterZ=0 NormalX=0 NormalY=0 NormalZ=1 AngleXU=0 Radius=1 StartAngle=5.82992 EndAngle=6.15188
    g82: ArcOfCircle CenterX=7.4 CenterY=1.5 CenterZ=0 NormalX=0 NormalY=0 NormalZ=1 AngleXU=0 Radius=1 StartAngle=3.27181 EndAngle=3.5951
    g83: LineSegment StartX=6.25982 StartY=1.5 StartZ=0 EndX=7.74018 EndY=1.5 EndZ=0
    g84: ArcOfCircle CenterX=8.25983 CenterY=1.35 CenterZ=0 NormalX=0 NormalY=0 NormalZ=1 AngleXU=0 Radius=0.149997 StartAngle=0.134719 EndAngle=1.57082
    g85: ArcOfCircle CenterX=9.74018 CenterY=1.35 CenterZ=0 NormalX=0 NormalY=0 NormalZ=1 AngleXU=0 Radius=0.15 StartAngle=1.5708 EndAngle=3.01411
    g86: ArcOfCircle CenterX=9 CenterY=1.30511 CenterZ=0 NormalX=0 NormalY=0 NormalZ=1 AngleXU=0 Radius=0.555048 StartAngle=3.59519 EndAngle=5.83002
    g87: ArcOfCircle CenterX=8.6 CenterY=1.5 CenterZ=0 NormalX=0 NormalY=0 NormalZ=1 AngleXU=0 Radius=1 StartAngle=5.82992 EndAngle=6.15188
    g88: ArcOfCircle CenterX=9.4 CenterY=1.5 CenterZ=0 NormalX=0 NormalY=0 NormalZ=1 AngleXU=0 Radius=1 StartAngle=3.27181 EndAngle=3.5951
    g89: LineSegment StartX=8.25982 StartY=1.5 StartZ=0 EndX=9.74018 EndY=1.5 EndZ=0
    g90: ArcOfCircle CenterX=10.2598 CenterY=1.35 CenterZ=0 NormalX=0 NormalY=0 NormalZ=1 AngleXU=0 Radius=0.149997 StartAngle=0.134719 EndAngle=1.57082
    g91: ArcOfCircle CenterX=11.7402 CenterY=1.35 CenterZ=0 NormalX=0 NormalY=0 NormalZ=1 AngleXU=0 Radius=0.15 StartAngle=1.5708 EndAngle=3.01411
    g92: ArcOfCircle CenterX=11 CenterY=1.30511 CenterZ=0 NormalX=0 NormalY=0 NormalZ=1 AngleXU=0 Radius=0.555048 StartAngle=3.59519 EndAngle=5.83002
    g93: ArcOfCircle CenterX=10.6 CenterY=1.5 CenterZ=0 NormalX=0 NormalY=0 NormalZ=1 AngleXU=0 Radius=1 StartAngle=5.82992 EndAngle=6.15188
    g94: ArcOfCircle CenterX=11.4 CenterY=1.5 CenterZ=0 NormalX=0 NormalY=0 NormalZ=1 AngleXU=0 Radius=1 StartAngle=3.27181 EndAngle=3.5951
    g95: LineSegment StartX=10.2598 StartY=1.5 StartZ=0 EndX=11.7402 EndY=1.5 EndZ=0
    g96: ArcOfCircle CenterX=12.2598 CenterY=1.35 CenterZ=0 NormalX=0 NormalY=0 NormalZ=1 AngleXU=0 Radius=0.149997 StartAngle=0.134719 EndAngle=1.57082
    g97: ArcOfCircle CenterX=13.7402 CenterY=1.35 CenterZ=0 NormalX=0 NormalY=0 NormalZ=1 AngleXU=0 Radius=0.15 StartAngle=1.5708 EndAngle=3.01411
    g98: ArcOfCircle CenterX=13 CenterY=1.30511 CenterZ=0 NormalX=0 NormalY=0 NormalZ=1 AngleXU=0 Radius=0.555048 StartAngle=3.59519 EndAngle=5.83002
    g99: ArcOfCircle CenterX=12.6 CenterY=1.5 CenterZ=0 NormalX=0 NormalY=0 NormalZ=1 AngleXU=0 Radius=1 StartAngle=5.82992 EndAngle=6.15188
    g100: ArcOfCircle CenterX=13.4 CenterY=1.5 CenterZ=0 NormalX=0 NormalY=0 NormalZ=1 AngleXU=0 Radius=1 StartAngle=3.27181 EndAngle=3.5951
    g101: LineSegment StartX=12.2598 StartY=1.5 StartZ=0 EndX=13.7402 EndY=1.5 EndZ=0
    g102: ArcOfCircle CenterX=14.2598 CenterY=1.35 CenterZ=0 NormalX=0 NormalY=0 NormalZ=1 AngleXU=0 Radius=0.149997 StartAngle=0.134719 EndAngle=1.57082
    g103: ArcOfCircle CenterX=15.7402 CenterY=1.35 CenterZ=0 NormalX=0 NormalY=0 NormalZ=1 AngleXU=0 Radius=0.15 StartAngle=1.5708 EndAngle=3.01411
    g104: ArcOfCircle CenterX=15 CenterY=1.30511 CenterZ=0 NormalX=0 NormalY=0 NormalZ=1 AngleXU=0 Radius=0.555048 StartAngle=3.59519 EndAngle=5.83002
    g105: ArcOfCircle CenterX=14.6 CenterY=1.5 CenterZ=0 NormalX=0 NormalY=0 NormalZ=1 AngleXU=0 Radius=1 StartAngle=5.82992 EndAngle=6.15188
    g106: ArcOfCircle CenterX=15.4 CenterY=1.5 CenterZ=0 NormalX=0 NormalY=0 NormalZ=1 AngleXU=0 Radius=1 StartAngle=3.27181 EndAngle=3.5951
    g107: LineSegment StartX=14.2598 StartY=1.5 StartZ=0 EndX=15.7402 EndY=1.5 EndZ=0
    g108: ArcOfCircle CenterX=16.2598 CenterY=1.35 CenterZ=0 NormalX=0 NormalY=0 NormalZ=1 AngleXU=0 Radius=0.149997 StartAngle=0.134719 EndAngle=1.57082
    g109: ArcOfCircle CenterX=17.7402 CenterY=1.35 CenterZ=0 NormalX=0 NormalY=0 NormalZ=1 AngleXU=0 Radius=0.15 StartAngle=1.5708 EndAngle=3.01411
    g110: ArcOfCircle CenterX=17 CenterY=1.30511 CenterZ=0 NormalX=0 NormalY=0 NormalZ=1 AngleXU=0 Radius=0.555048 StartAngle=3.59519 EndAngle=5.83002
    g111: ArcOfCircle CenterX=16.6 CenterY=1.5 CenterZ=0 NormalX=0 NormalY=0 NormalZ=1 AngleXU=0 Radius=1 StartAngle=5.82992 EndAngle=6.15188
    g112: ArcOfCircle CenterX=17.4 CenterY=1.5 CenterZ=0 NormalX=0 NormalY=0 NormalZ=1 AngleXU=0 Radius=1 StartAngle=3.27181 EndAngle=3.5951
    g113: LineSegment StartX=16.2598 StartY=1.5 StartZ=0 EndX=17.7402 EndY=1.5 EndZ=0
    g114: ArcOfCircle CenterX=18.2598 CenterY=1.35 CenterZ=0 NormalX=0 NormalY=0 NormalZ=1 AngleXU=0 Radius=0.149997 StartAngle=0.134719 EndAngle=1.57082
    g115: ArcOfCircle CenterX=19.7402 CenterY=1.35 CenterZ=0 NormalX=0 NormalY=0 NormalZ=1 AngleXU=0 Radius=0.15 StartAngle=1.5708 EndAngle=3.01411
    g116: ArcOfCircle CenterX=19 CenterY=1.30511 CenterZ=0 NormalX=0 NormalY=0 NormalZ=1 AngleXU=0 Radius=0.555048 StartAngle=3.59519 EndAngle=5.83002
    g117: ArcOfCircle CenterX=18.6 CenterY=1.5 CenterZ=0 NormalX=0 NormalY=0 NormalZ=1 AngleXU=0 Radius=1 StartAngle=5.82992 EndAngle=6.15188
    g118: ArcOfCircle CenterX=19.4 CenterY=1.5 CenterZ=0 NormalX=0 NormalY=0 NormalZ=1 AngleXU=0 Radius=1 StartAngle=3.27181 EndAngle=3.5951
    g119: LineSegment StartX=18.2598 StartY=1.5 StartZ=0 EndX=19.7402 EndY=1.5 EndZ=0
  constraints (140):
    c: Coincident(g0,g4)
    c: Coincident(g2,g4)
    c: Coincident(g2,g3)
    c: Coincident(g1,g3)
    c: Coincident(g5,g0)
    c: Tangent(g5,g1) = 1.5708
    c: Horizontal(g5)
    c: Coincident(g6,g10)
    c: Coincident(g12,g16)
    c: Coincident(g18,g22)
    c: Coincident(g24,g28)
    c: Coincident(g30,g34)
    c: Coincident(g36,g40)
    c: Coincident(g42,g46)
    c: Coincident(g48,g52)
    c: Coincident(g54,g58)
    c: Coincident(g60,g64)
    c: Coincident(g66,g70)
    c: Coincident(g72,g76)
    c: Coincident(g78,g82)
    c: Coincident(g84,g88)
    c: Coincident(g90,g94)
    c: Coincident(g96,g100)
    c: Coincident(g102,g106)
    c: Coincident(g108,g112)
    c: Coincident(g114,g118)
    c: Coincident(g8,g10)
    c: Coincident(g14,g16)
    c: Coincident(g20,g22)
    c: Coincident(g26,g28)
    c: Coincident(g32,g34)
    c: Coincident(g38,g40)
    c: Coincident(g44,g46)
    c: Coincident(g50,g52)
    c: Coincident(g56,g58)
    c: Coincident(g62,g64)
    c: Coincident(g68,g70)
    c: Coincident(g74,g76)
    c: Coincident(g80,g82)
    c: Coincident(g86,g88)
    c: Coincident(g92,g94)
    c: Coincident(g98,g100)
    c: Coincident(g104,g106)
    c: Coincident(g110,g112)
    c: Coincident(g116,g118)
    c: Coincident(g8,g9)
    c: Coincident(g14,g15)
    c: Coincident(g20,g21)
    c: Coincident(g26,g27)
    c: Coincident(g32,g33)
    c: Coincident(g38,g39)
    c: Coincident(g44,g45)
    c: Coincident(g50,g51)
    c: Coincident(g56,g57)
    c: Coincident(g62,g63)
    c: Coincident(g68,g69)
    c: Coincident(g74,g75)
    c: Coincident(g80,g81)
    c: Coincident(g86,g87)
    c: Coincident(g92,g93)
    c: Coincident(g98,g99)
    c: Coincident(g104,g105)
    c: Coincident(g110,g111)
    c: Coincident(g116,g117)
    c: Coincident(g7,g9)
    c: Coincident(g13,g15)
    c: Coincident(g19,g21)
    c: Coincident(g25,g27)
    c: Coincident(g31,g33)
    c: Coincident(g37,g39)
    c: Coincident(g43,g45)
    c: Coincident(g49,g51)
    c: Coincident(g55,g57)
    c: Coincident(g61,g63)
    c: Coincident(g67,g69)
    c: Coincident(g73,g75)
    c: Coincident(g79,g81)
    c: Coincident(g85,g87)
    c: Coincident(g91,g93)
    c: Coincident(g97,g99)
    c: Coincident(g103,g105)
    c: Coincident(g109,g111)
    c: Coincident(g115,g117)
    c: Coincident(g11,g6)
    c: Coincident(g17,g12)
    c: Coincident(g23,g18)
    c: Coincident(g29,g24)
    c: Coincident(g35,g30)
    c: Coincident(g41,g36)
    c: Coincident(g47,g42)
    c: Coincident(g53,g48)
    c: Coincident(g59,g54)
    c: Coincident(g65,g60)
    c: Coincident(g71,g66)
    c: Coincident(g77,g72)
    c: Coincident(g83,g78)
    c: Coincident(g89,g84)
    c: Coincident(g95,g90)
    c: Coincident(g101,g96)
    c: Coincident(g107,g102)
    c: Coincident(g113,g108)
    c: Coincident(g119,g114)
    c: Tangent(g11,g7) = 1.5708
    c: Tangent(g17,g13) = 1.5708
    c: Tangent(g23,g19) = 1.5708
    c: Tangent(g29,g25) = 1.5708
    c: Tangent(g35,g31) = 1.5708
    c: Tangent(g41,g37) = 1.5708
    c: Tangent(g47,g43) = 1.5708
    c: Tangent(g53,g49) = 1.5708
    c: Tangent(g59,g55) = 1.5708
    c: Tangent(g65,g61) = 1.5708
    c: Tangent(g71,g67) = 1.5708
    c: Tangent(g77,g73) = 1.5708
    c: Tangent(g83,g79) = 1.5708
    c: Tangent(g89,g85) = 1.5708
    c: Tangent(g95,g91) = 1.5708
    c: Tangent(g101,g97) = 1.5708
    c: Tangent(g107,g103) = 1.5708
    c: Tangent(g113,g109) = 1.5708
    c: Tangent(g119,g115) = 1.5708
    c: Horizontal(g11)
    c: Horizontal(g17)
    c: Horizontal(g23)
    c: Horizontal(g29)
    c: Horizontal(g35)
    c: Horizontal(g41)
    c: Horizontal(g47)
    c: Horizontal(g53)
    c: Horizontal(g59)
    c: Horizontal(g65)
    c: Horizontal(g71)
    c: Horizontal(g77)
    c: Horizontal(g83)
    c: Horizontal(g89)
    c: Horizontal(g95)
    c: Horizontal(g101)
    c: Horizontal(g107)
    c: Horizontal(g113)
    c: Horizontal(g119)
FEATURE [PartDesign::Pocket] Pocket017
  BaseFeature = -> Pad003
  Direction = (0,1,-2e-16)
  Length = 20
  Length2 = 5
  Profile = -> Sketch025
  ReferenceAxis = -> Sketch025 [N_Axis]
  Refine = true
  Suppressed = false
  Type = 0
FEATURE [Sketcher::SketchObject] Sketch026
  ArcFitTolerance = 1e-06
  AttachmentSupport = -> [XY_Plane011]
  FullyConstrained = false
  MakeInternals = false
  MapMode = 5
  sketch-geometry (9):
    g0: LineSegment StartX=-20 StartY=10 StartZ=0 EndX=-20 EndY=-10 EndZ=0
    g1: LineSegment StartX=-20 StartY=-10 StartZ=0 EndX=20 EndY=-10 EndZ=0
    g2: LineSegment StartX=20 StartY=-10 StartZ=0 EndX=20 EndY=10 EndZ=0
    g3: LineSegment StartX=20 StartY=10 StartZ=0 EndX=-20 EndY=10 EndZ=0
    g4: GeomPoint [constr] X=0 Y=0 Z=0
    g5: Circle CenterX=-8 CenterY=-8 CenterZ=0 NormalX=0 NormalY=0 NormalZ=1 AngleXU=0 Radius=1.6
    g6: Circle CenterX=8 CenterY=-8 CenterZ=0 NormalX=0 NormalY=0 NormalZ=1 AngleXU=0 Radius=1.6
    g7: Circle CenterX=-8 CenterY=8 CenterZ=0 NormalX=0 NormalY=0 NormalZ=1 AngleXU=0 Radius=1.6
    g8: Circle CenterX=8 CenterY=8 CenterZ=0 NormalX=0 NormalY=0 NormalZ=1 AngleXU=0 Radius=1.6
  constraints (8):
    c: Coincident(g0,g1)
    c: Coincident(g1,g2)
    c: Coincident(g2,g3)
    c: Coincident(g3,g0)
    c: Vertical(g0)
    c: Vertical(g2)
    c: Horizontal(g1)
    c: Horizontal(g3)
FEATURE [PartDesign::Pad] Pad004
  Direction = (0,0,1)
  Length = 1.5
  Length2 = 10
  Profile = -> Sketch026
  ReferenceAxis = -> Sketch026 [N_Axis]
  Refine = true
  Suppressed = false
  Type = 0
FEATURE [Sketcher::SketchObject] Sketch027
  ArcFitTolerance = 1e-06
  AttachmentSupport = -> [Pocket017]
  FullyConstrained = false
  MakeInternals = false
  MapMode = 5
  Placement = pos=(0,0,0) rot=(1,0,0;3.14159rad)
  sketch-geometry (5):
    g0: GeomPoint [constr] X=0 Y=0 Z=0
    g1: Circle CenterX=-8 CenterY=-8 CenterZ=0 NormalX=0 NormalY=0 NormalZ=1 AngleXU=0 Radius=1.6
    g2: Circle CenterX=8 CenterY=-8 CenterZ=0 NormalX=0 NormalY=0 NormalZ=1 AngleXU=0 Radius=1.6
    g3: Circle CenterX=-8 CenterY=8 CenterZ=0 NormalX=0 NormalY=0 NormalZ=1 AngleXU=0 Radius=1.6
    g4: Circle CenterX=8 CenterY=8 CenterZ=0 NormalX=0 NormalY=0 NormalZ=1 AngleXU=0 Radius=1.6
FEATURE [PartDesign::Pocket] Pocket018
  BaseFeature = -> Pocket017
  Direction = (0,0,1)
  Length = 1.5
  Length2 = 5
  Profile = -> Sketch027
  ReferenceAxis = -> Sketch027 [N_Axis]
  Refine = true
  Suppressed = false
  Type = 0
FEATURE [PartDesign::Body] Body003
  AllowCompound = false
  Group = -> [Sketch024,Pad003,Sketch025,Pocket017,Sketch027,Pocket018]
  Origin = -> Origin010
  Tip = -> Pocket018
FEATURE [App::Part] Part003  label="Base"
  Group = -> [Body003]
  Origin = -> Origin009
  Placement = pos=(0,0,29) rot=(0,0,1;0rad)
FEATURE [Sketcher::SketchObject] Sketch028
  ArcFitTolerance = 1e-06
  AttachmentSupport = -> [Pad004]
  FullyConstrained = false
  MakeInternals = false
  MapMode = 5
  Placement = pos=(-20,0,0) rot=(0.57735,-0.57735,-0.57735;2.0944rad)
  sketch-geometry (4):
    g0: LineSegment StartX=-3.1 StartY=1 StartZ=0 EndX=-3.1 EndY=0 EndZ=0
    g1: LineSegment StartX=-3.1 StartY=0 StartZ=0 EndX=3.1 EndY=0 EndZ=0
    g2: LineSegment StartX=3.1 StartY=0 StartZ=0 EndX=3.1 EndY=1 EndZ=0
    g3: LineSegment StartX=3.1 StartY=1 StartZ=0 EndX=-3.1 EndY=1 EndZ=0
  constraints (8):
    c: Coincident(g0,g1)
    c: Coincident(g1,g2)
    c: Coincident(g2,g3)
    c: Coincident(g3,g0)
    c: Vertical(g0)
    c: Vertical(g2)
    c: Horizontal(g1)
    c: Horizontal(g3)
FEATURE [PartDesign::Pocket] Pocket019
  BaseFeature = -> Pad004
  Direction = (1,0,0)
  Length = 40
  Length2 = 5
  Profile = -> Sketch028
  ReferenceAxis = -> Sketch028 [N_Axis]
  Refine = true
  Suppressed = false
  Type = 0
FEATURE [PartDesign::Body] Body004
  AllowCompound = false
  Group = -> [Sketch026,Pad004,Sketch028,Pocket019]
  Origin = -> Origin011
  Tip = -> Pocket019
FEATURE [App::Part] Part004  label="BaseCover"
  Group = -> [Body004]
  Origin = -> Origin012
  Placement = pos=(0,0,32) rot=(0,0,1;0rad)
FEATURE [Assembly::JointGroup] Joints
FEATURE [Assembly::AssemblyObject] Assembly
  Group = -> [Joints,Part004,Part003,Part,Part__Mirroring,Part002,Part001]
  Origin = -> Origin013
  Type = Assembly
